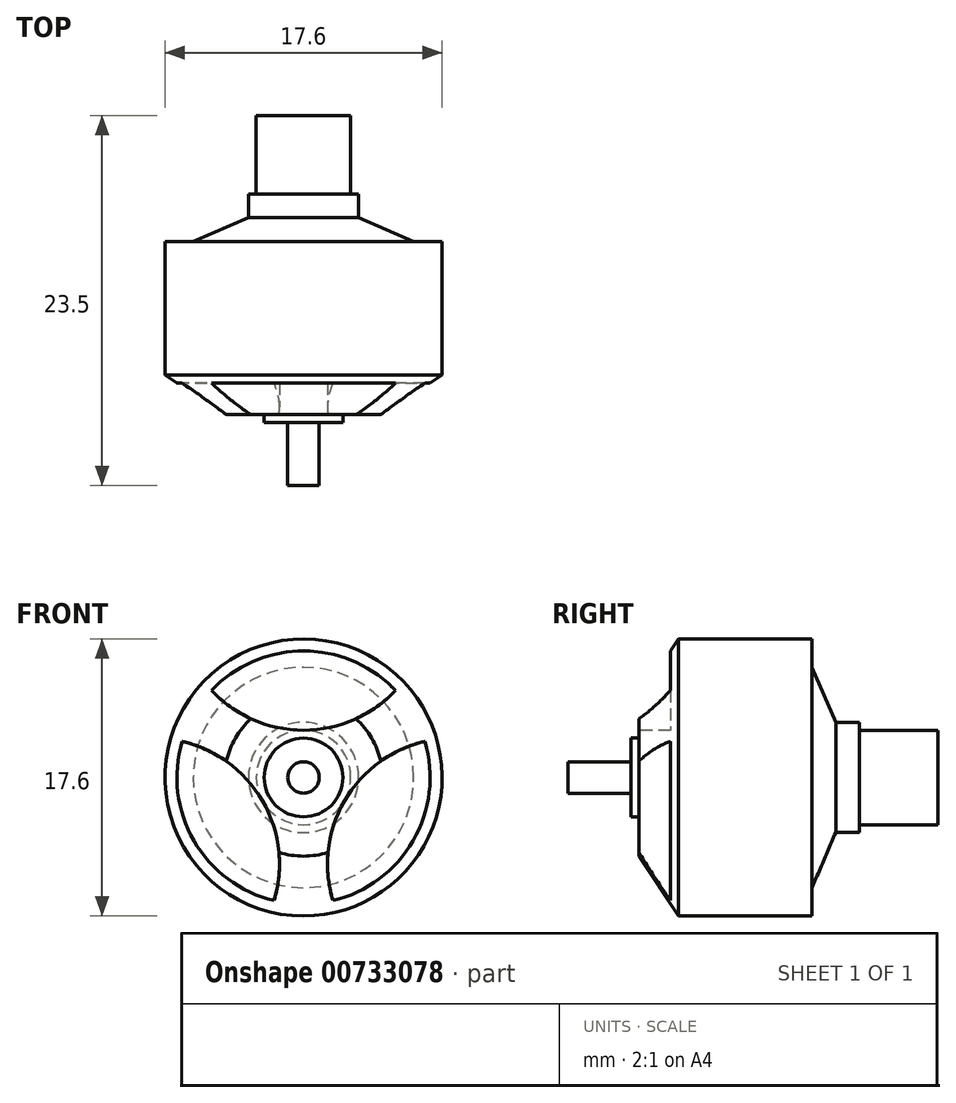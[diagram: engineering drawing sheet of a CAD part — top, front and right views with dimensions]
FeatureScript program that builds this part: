
annotation { "Feature Type Name" : "Feature", "Feature Type Description" : "" }
export const myFeature = defineFeature(function(context is Context, id is Id, definition is map)
    precondition{}
    {
        {
            var Q0;
            Q0=qCreatedBy(makeId("Right.planeOp"),FACE);
            var sketch = newSketch(context, id + "F0", { "sketchPlane" : qUnion([Q0])});
            skLineSegment(sketch, "E0", {"start": v(0, 0) * mm, "end": v(0, 3) * mm});
            skLineSegment(sketch, "E1", {"start": v(0, 3) * mm, "end": v(-5, 3) * mm});
            skLineSegment(sketch, "E2", {"start": v(-5, 3) * mm, "end": v(-5, 3.5) * mm});
            skLineSegment(sketch, "E3", {"start": v(-5, 3.5) * mm, "end": v(-6.5, 3.5) * mm});
            skLineSegment(sketch, "E4", {"start": v(-6.5, 3.5) * mm, "end": v(-8, 7) * mm});
            skLineSegment(sketch, "E5", {"start": v(-8, 7) * mm, "end": v(-8, 8.8) * mm});
            skLineSegment(sketch, "E6", {"start": v(-8, 8.8) * mm, "end": v(-16.5, 8.8) * mm});
            skLineSegment(sketch, "E7", {"start": v(-16.5, 8.8) * mm, "end": v(-19, 5) * mm});
            skLineSegment(sketch, "E8", {"start": v(-19, 5) * mm, "end": v(-19, 2.5) * mm});
            skLineSegment(sketch, "E9", {"start": v(-19, 2.5) * mm, "end": v(-19.5, 2.5) * mm});
            skLineSegment(sketch, "E10", {"start": v(-19.5, 2.5) * mm, "end": v(-19.5, 1) * mm});
            skLineSegment(sketch, "E11", {"start": v(-19.5, 1) * mm, "end": v(-23.5, 1) * mm});
            skLineSegment(sketch, "E12", {"start": v(-23.5, 1) * mm, "end": v(-23.5, 0) * mm});
            skLineSegment(sketch, "E13", {"start": v(-23.5, 0) * mm, "end": v(0, 0) * mm});
            skSolve(sketch);
        }
        {
            var Q0;
            Q0=makeQuery(id+"F0.imprint","IMPRINT",FACE,{"disambiguationData":[TD([[makeQuery(id+"F0.imprint","IMPRINT",EDGE,{"derivedFrom":sQuery(id+"F0.wireOp",EDGE,"E0")}),1.0]])]});
            var Q1;
            Q1=sQuery(id+"F0.wireOp",EDGE,"E13");
            revolve(context, id + "F1", {"surfaceOperationType" : NewSurfaceOperationType.NEW, "entities" : qUnion([Q0]), "axis" : qUnion([Q1]), "revolveType" : RevolveType.FULL});
        }
        {
            var Q0;
            Q0=makeQuery(id+"F1.opRevolve","SWEPT_FACE",FACE,{"disambiguationData":[OSD([sQuery(id+"F0.wireOp",EDGE,"E8")])]});
            var sketch = newSketch(context, id + "F2", { "sketchPlane" : qUnion([Q0])});
            skCircle(sketch, "E14", {"center": v(0, 11) * mm, "radius": 8 * mm});
            skLineSegment(sketch, "E15", {"start": v(-6, 5.7) * mm, "end": v(6, 5.7) * mm, "construction": true});
            skCircle(sketch, "E16.1.0", {"center": v(-9.53, -5.5) * mm, "radius": 8 * mm});
            skCircle(sketch, "E16.2.0", {"center": v(9.53, -5.5) * mm, "radius": 8 * mm});
            skPoint(sketch, "E16.center", {"position": v(0, 0) * mm});
            skSolve(sketch);
        }
        {
            var Q0;
            Q0 = qSketchRegion(id + "F2", true);
            extrude(context, id + "F3", {"entities" : qUnion([Q0]), "operationType" : NewBodyOperationType.REMOVE, "oppositeDirection" : true, "depth" : 2 * mm, "offsetDistance" : 25 * mm});
        }
    });
